# Revit family: Plumbing_Drainage_AXOR_42541XXX-Flexaplus-Complete-set_waste-overflow-set-for-bathtubs
name_source: partatom
category: Plumbing Fixtures
units: mm (PartAtom-declared; Revit-internal decimal feet)

## family parameters
Cut with Voids When Loaded = No
Host = Face
Maintain Annotation Orientation = No
OmniClass Number = 23.31.15.17.23
OmniClass Title = Bathtub Drains
Part Type = Normal
Room Calculation Point = No
Round Connector Dimension = Use Diameter
Shared = No

## types (5) — shared parameters
Connector Description = Water Outlet 50mm
Date Updated = 2025/01/13
Description = Flexaplus Complete set basic set and finish set waste and overflow set for bathtubs
Diameter = 50 mm
Manufacturer = Hansgrohe
Material 2 = AXOR - Plastic - Black
Material 3 = AXOR - Plastic - Grey
Model = 42541XXX
Product Page URL = https://www.axor-design.com
Product data url = https://bimobject.com
URL = https://www.hansgrohe.com
Version = 1
zero-valued in all types: Default Elevation

## per-type parameters (varying)
| type | Material 1 |
| 700 Matt White | AXOR - Metal - 700 Matt White |
| 670 Matt Black | AXOR - Metal - 670 Matt Black |
| 340 Brushed Black Chrome | AXOR - Metal - 340 Brushed Black Chrome |
| 140 Brushed Bronze | AXOR - Metal - 140 Brushed Bronze |
| 000 Chrome | AXOR - Metal - 000 Chrome |

## geometry (parser evidence)
native form markers: Sweep x2
no freeform markers — native parametric forms only
